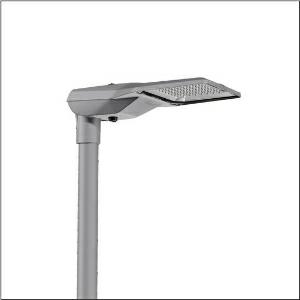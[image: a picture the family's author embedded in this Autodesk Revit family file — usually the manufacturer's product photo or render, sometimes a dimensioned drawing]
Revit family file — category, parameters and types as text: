
# Revit family: streetlight_sl_21_midi___pl52_5xe3h43t08lb_3b1c
name_source: partatom
category: Lighting Fixtures
units: mm (PartAtom-declared; Revit-internal decimal feet)

## family parameters
Cut with Voids When Loaded = No
Host = Face
Light Source = No
Part Type = Normal
Room Calculation Point = No
Round Connector Dimension = Use Diameter
Shared = No

## types (1)
- --- (1 x LED, 14690 lm, 99.6 W, 4000K)
    Apparent Load = 100 VA
    CIE Flux Codes = 27 59 98 100 100
    Color Rendering = 70
    Color Temperature = 4000K
    Default Elevation = 1800 mm
    Description = Streetlight SL 21 midi, mast luminaire, primary light control with lens, of PMMA, primary optical cover: cover, of toughened safety glass, transparent, light distribution: PL52, light emission: direct distribution, primary light characteristic: asymmetric, installation type: side-entry, post-top, LED, High Power LED, rated luminous flux: 14.690lm, luminous efficacy: 148lm/W, light colour: 740, colour temperature: 4000K, control gear: D4i, control: overheat protection, constant luminous flux control, time-dependent luminous flux control, flexible luminous flux parameterisation, pre-setting: logarithmic dimming characteristic, mains connection: 230..240V, AC, 50/60Hz, start of lifetime: 100W, end of service life: 102W, reduction: 46W, luminaire housing, of diecast aluminium, powder-coated, SITECO metallic grey (DB 702S), corrosivity category C5 high according to DIN EN ISO 12944, please order mast flange separately, inclination adjustable: 0°, 5°, 10°, 15°, sealing non-destructively replaceable, multi-level sealing system, length: 644mm, width: 335mm, height: 110mm, mast flange for spigot size: 42mm (side-entry): 5XC10008XM4, 60/48mm (side-entry/post-top): 5XC10108XM2, 76/60mm (side-entry/post-top): 5XC10108XM1, mounting height: 4..8m, Smart Interface below and above, protection rating (complete): IP66, insulation class (complete): insulation class II (safety insulation), certification: CE, ENEC, ENEC+, VDE, impact resistance: IK10, permissible operating ambient temperature for outdoor applications: -40..+50°C, standard-compliant lighting for roads and squares, packaging unit: 1 piece

Light Distribution: PL52
    Height = 111 mm
    Lamp = 1 x LED
    Lamp Light Flux = 14690 lm
    Lamp Power = 99.6 W
    Lamp count = 1
    Length = 644 mm
    Luminous efficacy = 147 lm/W
    Manufacturer = Siteco
    ModVariant = No
    Model = 5XE3H43T08LB
    Number of Poles = 1
    OnlyDefault = Yes
    Power Factor = 1
    Product Name = Streetlight SL 21 midi | PL52
    Product group = mast luminaire | pylon top
    ProductGroupID = 6100
    Protection Class = Protection class II
    Protection Degree = IP 66
    RLX_Detail_Level = 1
    RLX_Emergency_Light_Flux = 0 lm
    RLX_Emergency_Type = 0
    RLX_Emergency_Type_DB = No
    RlxData = <blob elided: 36521 chars, md5=63939cb4>
    Socket = socket
    Standby Power = 0 W
    System Light Flux = 14690 lm
    System Power = 100 W
    Type Comments = factory setting: luminous flux: 100 % | dim-lin: 254 | 1020 mA
    Type Image = l_1004304.jpg
    URL = http://relux.com
    VarID = @adj_032071
    Voltage = 0 V
    Weight = 0.00 kg
    Width = 336 mm

## geometry (parser evidence)
native form markers: Blend x4, Sweep x8
no freeform markers — native parametric forms only
